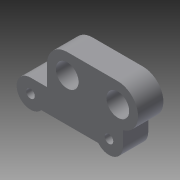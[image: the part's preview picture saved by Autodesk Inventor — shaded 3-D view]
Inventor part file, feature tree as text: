
AUTODESK INVENTOR PART (.ipt)
format: ipt  version: 2015 (Build 190159000, 159)  size: 128,000 bytes
history: native  units: mm
features: sketch x3, hole x2, extrude x1
ambient origin geometry x8: Origin, YZ Plane, XZ Plane, XY Plane, X Axis, Y Axis, Z Axis, Center Point
bodies: Solid1 (feature_tree)
feature tree (6):
  extrude  "Extrusion1"  Depth=16.0mm
  hole  "Hole1"  [1 undecoded]
  hole  "Hole2"  [1 undecoded]
  sketch  "Sketch1"  dims[d0=16.0mm d1=11.0mm]
  sketch  "Sketch3"  dims[d3=9.0mm d4=20.0mm]
  sketch  "Sketch5"  dims[d6=2.0mm d7=31.0mm d8=10.0mm d9=0.0mm d12=20.0mm d13=9.0mm d14=6.0mm d15=4.0mm d16=2.0mm d17=90.0deg d18=8.0mm d19=20.594885mm d21=0.0mm d22=5.5mm d23=0.0mm d24=3.4mm d25=6.0mm d26=7.0mm d27=3.0mm d28=90.0deg d29=8.0mm d30=20.594885mm]
note: 2 required parameter values undecoded (feature->parameter linkage not recoverable at this tier; creation-order binding heuristic only, values carry confidence <= 0.55)
